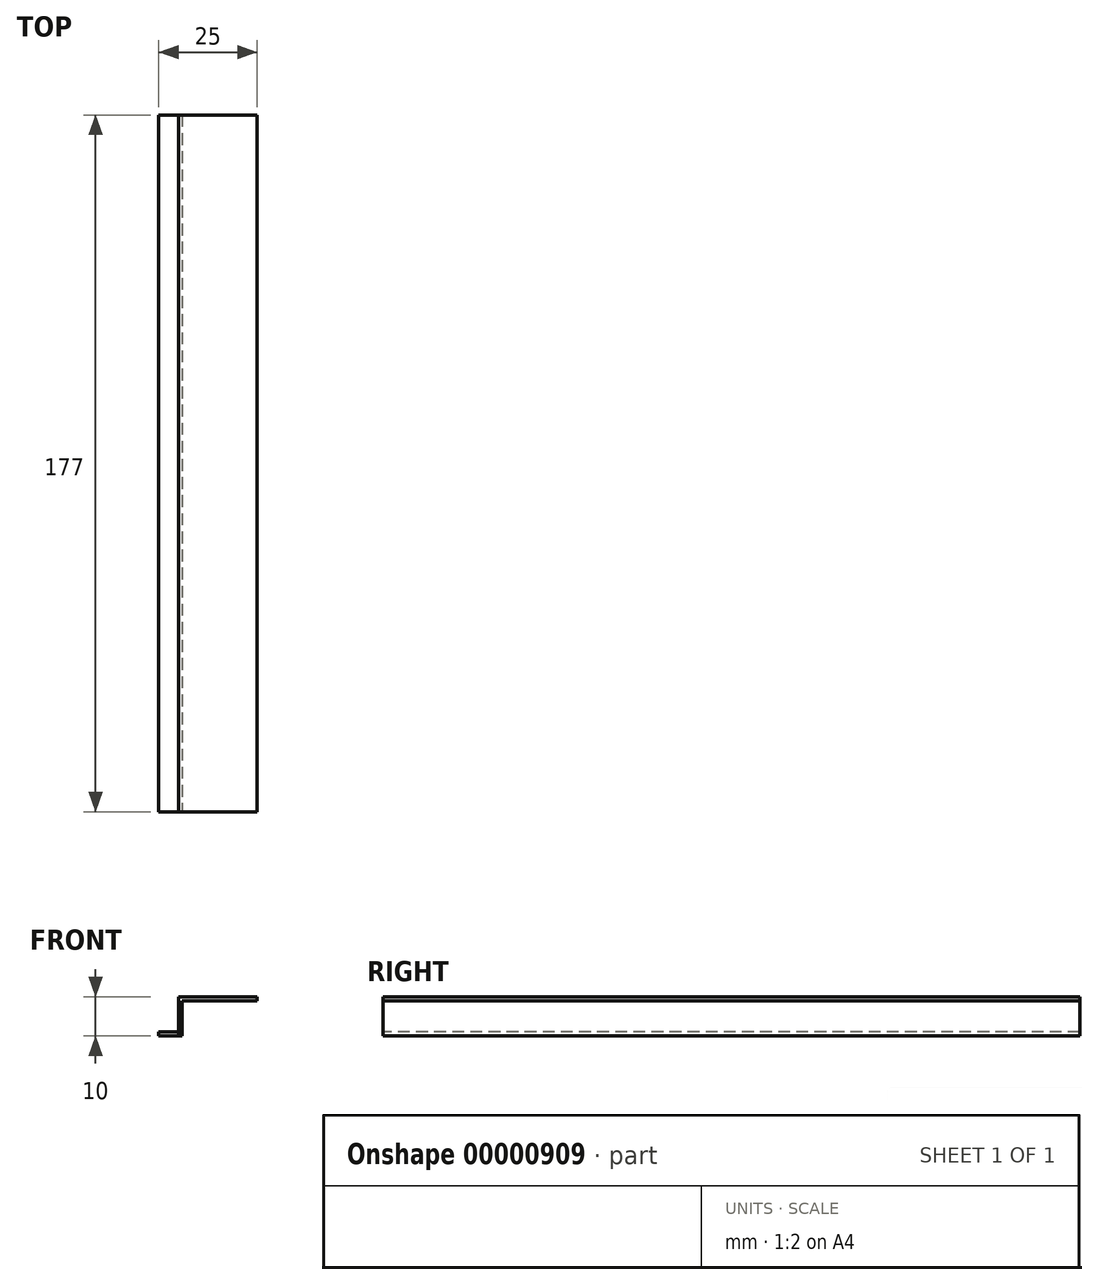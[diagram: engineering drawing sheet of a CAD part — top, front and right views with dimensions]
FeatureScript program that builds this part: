
annotation { "Feature Type Name" : "Feature", "Feature Type Description" : "" }
export const myFeature = defineFeature(function(context is Context, id is Id, definition is map)
    precondition{}
    {
        {
            var Q0;
            Q0=qCreatedBy(makeId("Front.planeOp"),FACE);
            var sketch = newSketch(context, id + "F0", { "sketchPlane" : qUnion([Q0])});
            skLineSegment(sketch, "E0", {"start": v(0, 0) * mm, "end": v(5, 0) * mm});
            skLineSegment(sketch, "E1", {"start": v(5, 0) * mm, "end": v(5, 10) * mm});
            skLineSegment(sketch, "E2", {"start": v(5, 10) * mm, "end": v(25, 10) * mm});
            skSolve(sketch);
        }
        {
            var Q0;
            Q0=sQuery(id+"F0.wireOp",EDGE,"E2");
            var Q1;
            Q1=sQuery(id+"F0.wireOp",EDGE,"E1");
            var Q2;
            Q2=sQuery(id+"F0.wireOp",EDGE,"E0");
            extrude(context, id + "F1", {"bodyType" : ToolBodyType.SURFACE, "surfaceEntities" : qUnion([Q0, Q1, Q2]), "depth" : 177 * mm});
        }
        {
            var Q0;
            Q0=makeQuery(id+"F1.opExtrude","SWEPT_FACE",FACE,{"disambiguationData":[OSD([sQuery(id+"F0.wireOp",EDGE,"E2")])]});
            extrude(context, id + "F2", {"entities" : qUnion([Q0]), "depth" : 1 * mm});
        }
        {
            var Q0;
            Q0=makeQuery(id+"F1.opExtrude","SWEPT_FACE",FACE,{"disambiguationData":[OSD([sQuery(id+"F0.wireOp",EDGE,"E1")])]});
            extrude(context, id + "F3", {"entities" : qUnion([Q0]), "operationType" : NewBodyOperationType.ADD, "depth" : 1 * mm});
        }
        {
            var Q0;
            Q0=makeQuery(id+"F1.opExtrude","SWEPT_FACE",FACE,{"disambiguationData":[OSD([sQuery(id+"F0.wireOp",EDGE,"E0")])]});
            extrude(context, id + "F4", {"entities" : qUnion([Q0]), "oppositeDirection" : true, "depth" : 1 * mm});
        }
    });
